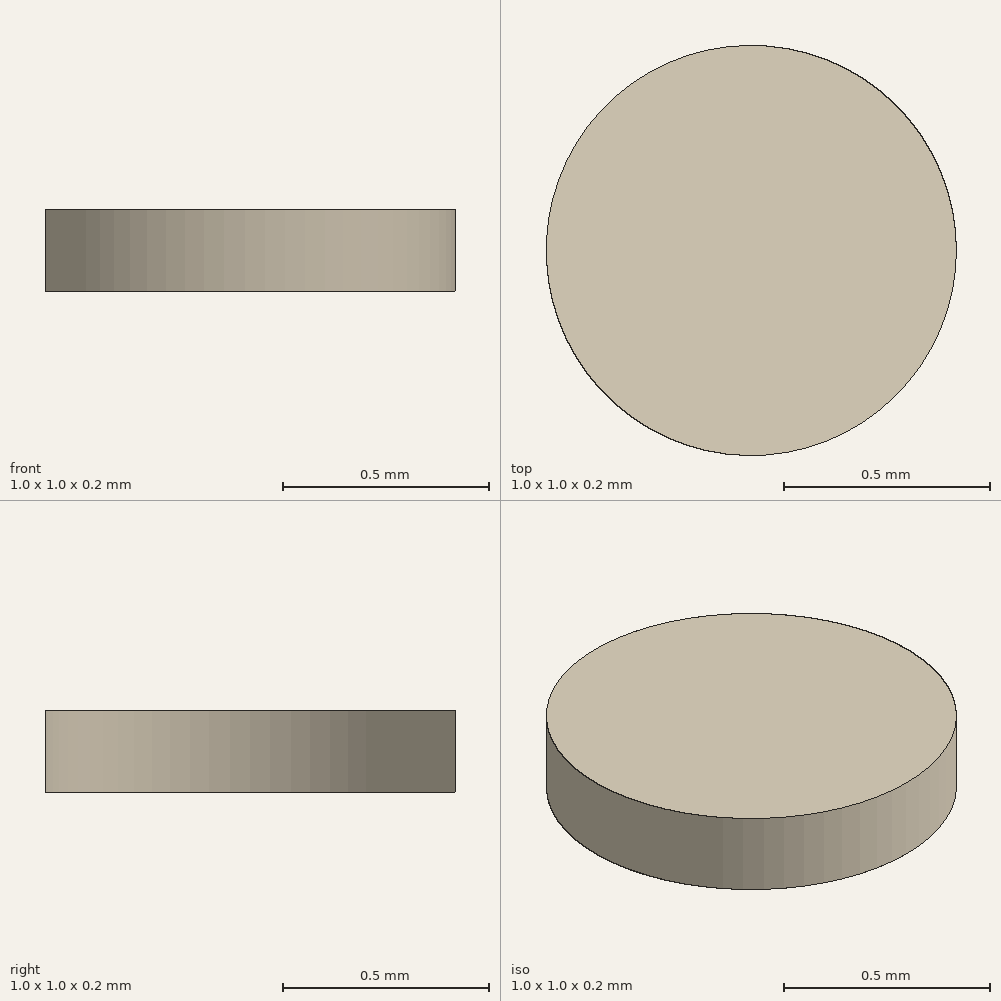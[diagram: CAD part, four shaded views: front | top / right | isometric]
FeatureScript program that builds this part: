
annotation { "Feature Type Name" : "Feature", "Feature Type Description" : "" }
export const myFeature = defineFeature(function(context is Context, id is Id, definition is map)
    precondition{}
    {
        {
            var Q0;
            Q0=qCreatedBy(makeId("Top.planeOp"),FACE);
            var sketch = newSketch(context, id + "F0", { "sketchPlane" : qUnion([Q0])});
            skCircle(sketch, "E0", {"center": v(0, 0) * mm, "radius": 0.5 * mm});
            skSolve(sketch);
        }
        {
            var Q0;
            Q0 = qSketchRegion(id + "F0", true);
            extrude(context, id + "F1", {"entities" : qUnion([Q0]), "depth" : .2 * mm, "offsetDistance" : 25 * mm});
        }
    });
